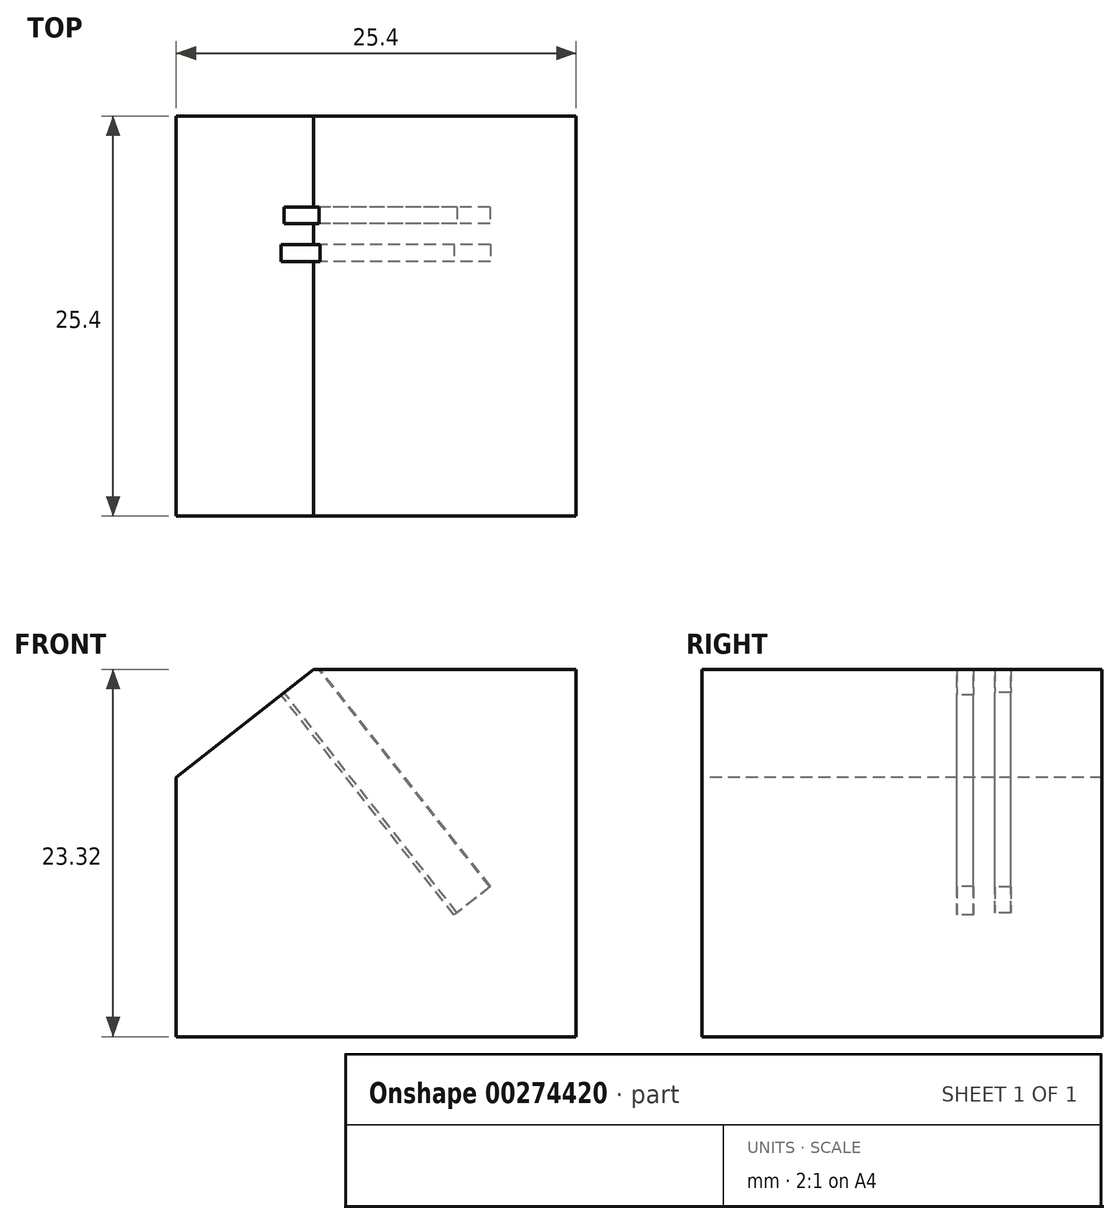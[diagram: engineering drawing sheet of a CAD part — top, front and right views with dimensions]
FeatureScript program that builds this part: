
annotation { "Feature Type Name" : "Feature", "Feature Type Description" : "" }
export const myFeature = defineFeature(function(context is Context, id is Id, definition is map)
    precondition{}
    {
        {
            var Q0;
            Q0=qCreatedBy(makeId("Front.planeOp"),FACE);
            var sketch = newSketch(context, id + "F0", { "sketchPlane" : qUnion([Q0])});
            skLineSegment(sketch, "E0.bottom", {"start": v(-12.7, 11.66) * mm, "end": v(12.7, 11.66) * mm});
            skLineSegment(sketch, "E0.top", {"start": v(-12.7, -11.66) * mm, "end": v(12.7, -11.66) * mm});
            skLineSegment(sketch, "E0.left", {"start": v(-12.7, 11.66) * mm, "end": v(-12.7, -11.66) * mm});
            skLineSegment(sketch, "E0.right", {"start": v(12.7, 11.66) * mm, "end": v(12.7, -11.66) * mm});
            skPoint(sketch, "E0.middle", {"position": v(0, 0) * mm});
            skSolve(sketch);
        }
        {
            var Q0;
            Q0=makeQuery(id+"F0.imprint","IMPRINT",FACE,{"disambiguationData":[TD([[makeQuery(id+"F0.imprint","IMPRINT",EDGE,{"derivedFrom":sQuery(id+"F0.wireOp",EDGE,"E0.bottom")}),-1.0]])]});
            extrude(context, id + "F1", {"entities" : qUnion([Q0]), "endBound" : BoundingType.SYMMETRIC, "depth" : 25.4 * mm, "offsetDistance" : 25.4 * mm});
        }
        {
            var Q0;
            Q0=makeQuery(id+"F1.opExtrude","CAP_FACE",FACE,{"disambiguationData":[OSD([sQuery(id+"F0.wireOp",EDGE,"E0.bottom"),sQuery(id+"F0.wireOp",EDGE,"E0.top"),sQuery(id+"F0.wireOp",EDGE,"E0.left"),sQuery(id+"F0.wireOp",EDGE,"E0.right")])],"isStart":false});
            var sketch = newSketch(context, id + "F2", { "sketchPlane" : qUnion([Q0])});
            skLineSegment(sketch, "E1", {"start": v(-3.98, 11.66) * mm, "end": v(-12.7, 4.81) * mm});
            skSolve(sketch);
        }
        {
            var Q0;
            {var subQ0=sQuery(id+"F2.wireOp",EDGE,"E1");Q0=makeQuery(id+"F2.imprint","IMPRINT",FACE,{"disambiguationData":[TD([[makeQuery(id+"F2.imprint","IMPRINT",EDGE,{"derivedFrom":subQ0}),-1.0]])]});}
            extrude(context, id + "F3", {"entities" : qUnion([Q0]), "operationType" : NewBodyOperationType.REMOVE, "oppositeDirection" : true, "depth" : 25.4 * mm, "offsetDistance" : 25.4 * mm});
        }
        {
            var Q0;
            Q0=makeQuery(id+"F3.boolean.opBoolean","COPY",FACE,{"derivedFrom":makeQuery(id+"F3.opExtrude","SWEPT_FACE",FACE,{"disambiguationData":[OSD([sQuery(id+"F2.wireOp",EDGE,"E1")])]})});
            var sketch = newSketch(context, id + "F4", { "sketchPlane" : qUnion([Q0])});
            skLineSegment(sketch, "E2.bottom", {"start": v(4.34, 6.91) * mm, "end": v(1.7, 6.91) * mm});
            skLineSegment(sketch, "E2.top", {"start": v(4.34, 5.89) * mm, "end": v(1.7, 5.89) * mm});
            skLineSegment(sketch, "E2.left", {"start": v(4.34, 6.91) * mm, "end": v(4.34, 5.89) * mm});
            skLineSegment(sketch, "E2.right", {"start": v(1.7, 6.91) * mm, "end": v(1.7, 5.89) * mm});
            skLineSegment(sketch, "E3.bottom", {"start": v(4.4, 4.55) * mm, "end": v(1.46, 4.55) * mm});
            skLineSegment(sketch, "E3.top", {"start": v(4.4, 3.47) * mm, "end": v(1.46, 3.47) * mm});
            skLineSegment(sketch, "E3.left", {"start": v(4.4, 4.55) * mm, "end": v(4.4, 3.47) * mm});
            skLineSegment(sketch, "E3.right", {"start": v(1.46, 4.55) * mm, "end": v(1.46, 3.47) * mm});
            skSolve(sketch);
        }
        {
            var Q0;
            Q0=makeQuery(id+"F4.imprint","IMPRINT",FACE,{"disambiguationData":[TD([[makeQuery(id+"F4.imprint","IMPRINT",EDGE,{"derivedFrom":sQuery(id+"F4.wireOp",EDGE,"E2.bottom")}),1.0]])]});
            var Q1;
            Q1=makeQuery(id+"F4.imprint","IMPRINT",FACE,{"disambiguationData":[TD([[makeQuery(id+"F4.imprint","IMPRINT",EDGE,{"derivedFrom":sQuery(id+"F4.wireOp",EDGE,"E3.bottom")}),1.0]])]});
            extrude(context, id + "F5", {"entities" : qUnion([Q0, Q1]), "operationType" : NewBodyOperationType.REMOVE, "oppositeDirection" : true, "depth" : 17.78 * mm, "offsetDistance" : 25.4 * mm});
        }
        {
            var Q0;
            Q0=makeQuery(id+"F1.opExtrude","CAP_FACE",FACE,{"disambiguationData":[OSD([sQuery(id+"F0.wireOp",EDGE,"E0.bottom"),sQuery(id+"F0.wireOp",EDGE,"E0.top"),sQuery(id+"F0.wireOp",EDGE,"E0.left"),sQuery(id+"F0.wireOp",EDGE,"E0.right")])],"isStart":false});
            var sketch = newSketch(context, id + "F6", { "sketchPlane" : qUnion([Q0])});
            skLineSegment(sketch, "E4.bottom", {"start": v(-0.86, 1.17) * mm, "end": v(-21.52, 1.17) * mm});
            skLineSegment(sketch, "E4.top", {"start": v(-0.86, 16.26) * mm, "end": v(-21.52, 16.26) * mm});
            skLineSegment(sketch, "E4.left", {"start": v(-0.86, 1.17) * mm, "end": v(-0.86, 16.26) * mm});
            skLineSegment(sketch, "E4.right", {"start": v(-21.52, 1.17) * mm, "end": v(-21.52, 16.26) * mm});
            skSolve(sketch);
        }
        {
            var Q0;
            {var subQ2=sQuery(id+"F6.wireOp",EDGE,"E4.top");Q0=makeQuery(id+"F6.imprint","IMPRINT",FACE,{"disambiguationData":[TD([[makeQuery(id+"F6.imprint","IMPRINT",EDGE,{"derivedFrom":subQ2}),1.0]])]});}
            var Q1;
            {var subQ0=makeQuery(id+"F3.boolean.opBoolean","COPY",EDGE,{"derivedFrom":makeQuery(id+"F3.opExtrude","CAP_EDGE",EDGE,{"disambiguationData":[OSD([sQuery(id+"F2.wireOp",EDGE,"E1")])],"isStart":true})});Q1=makeQuery(id+"F6.imprint","IMPRINT",FACE,{"disambiguationData":[TD([[makeQuery(id+"F6.imprint","IMPRINT",EDGE,{"derivedFrom":subQ0}),1.0]])]});}
            extrude(context, id + "F7", {"entities" : qUnion([Q0, Q1]), "operationType" : NewBodyOperationType.REMOVE, "oppositeDirection" : true, "depth" : 25.4 * mm, "offsetDistance" : 25.4 * mm});
        }
    });
